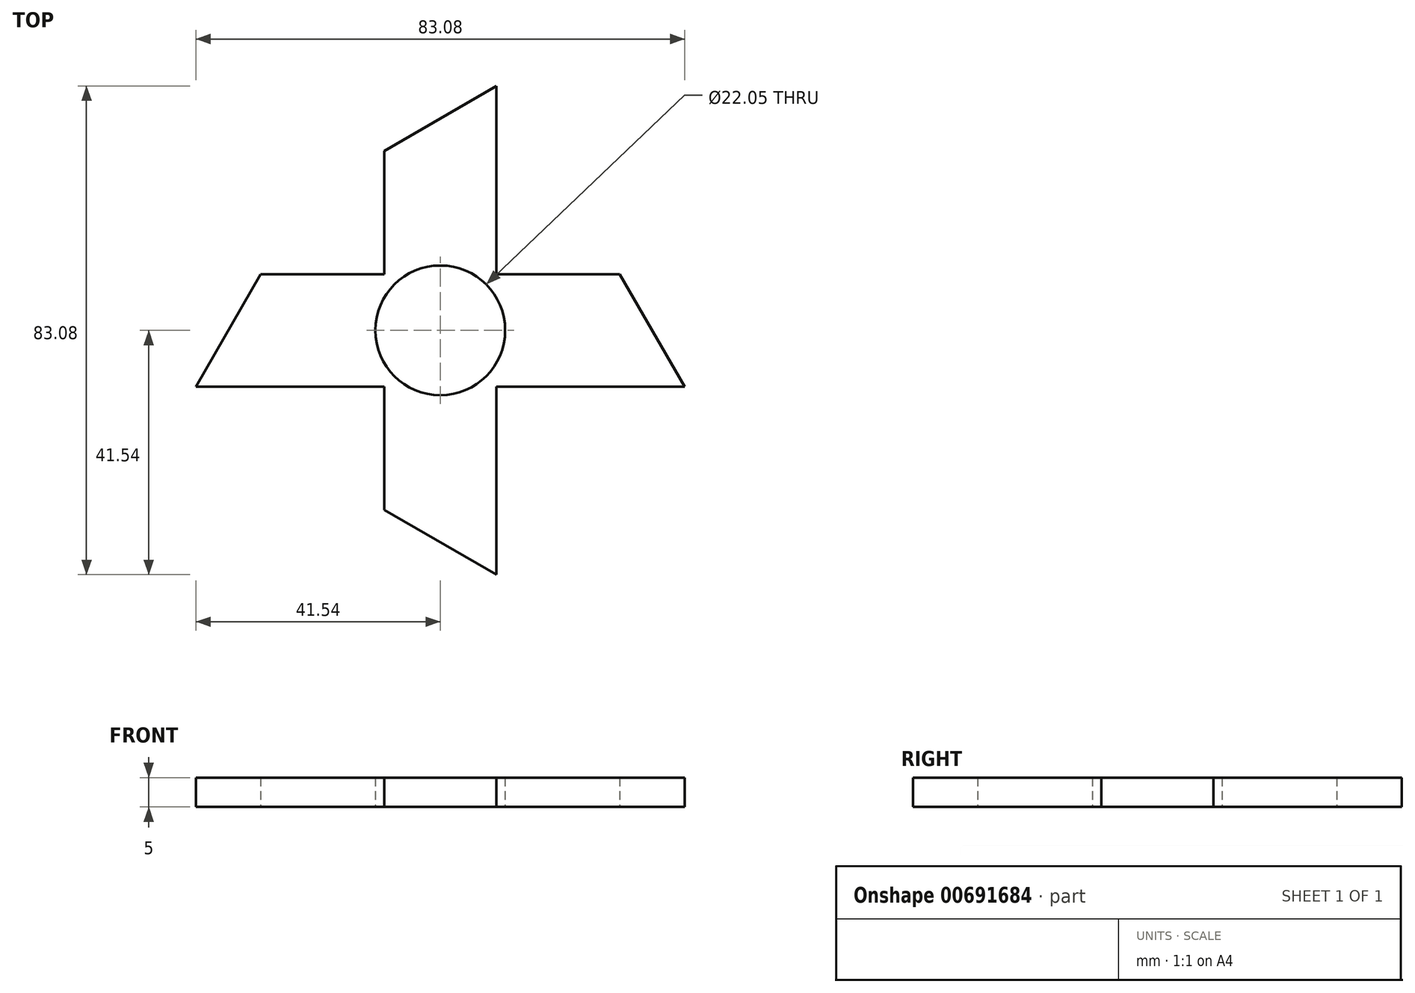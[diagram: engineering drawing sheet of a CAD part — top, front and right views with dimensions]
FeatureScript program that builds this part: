
annotation { "Feature Type Name" : "Feature", "Feature Type Description" : "" }
export const myFeature = defineFeature(function(context is Context, id is Id, definition is map)
    precondition{}
    {
        {
            var Q0;
            Q0=qCreatedBy(makeId("Top.planeOp"),FACE);
            var sketch = newSketch(context, id + "F0", { "sketchPlane" : qUnion([Q0])});
            skCircle(sketch, "E0", {"center": v(0, 0) * mm, "radius": 11.03 * mm});
            skLineSegment(sketch, "E1", {"start": v(0, 0) * mm, "end": v(0, 11.03) * mm});
            skLineSegment(sketch, "E2", {"start": v(-9.55, 5.51) * mm, "end": v(-9.55, 30.51) * mm});
            skPoint(sketch, "E2.startSnap0", {"position": v(0, 5.51) * mm});
            skLineSegment(sketch, "E3", {"start": v(9.55, 5.51) * mm, "end": v(9.55, 30.51) * mm});
            skLineSegment(sketch, "E4", {"start": v(-9.55, 30.51) * mm, "end": v(9.55, 30.51) * mm});
            skLineSegment(sketch, "E5.1.0", {"start": v(-5.51, 9.55) * mm, "end": v(-30.51, 9.55) * mm});
            skLineSegment(sketch, "E5.1.1", {"start": v(-30.51, -9.55) * mm, "end": v(-30.51, 9.55) * mm});
            skLineSegment(sketch, "E5.1.2", {"start": v(-5.51, -9.55) * mm, "end": v(-30.51, -9.55) * mm});
            skLineSegment(sketch, "E5.2.0", {"start": v(-9.55, -5.51) * mm, "end": v(-9.55, -30.51) * mm});
            skLineSegment(sketch, "E5.2.1", {"start": v(9.55, -30.51) * mm, "end": v(-9.55, -30.51) * mm});
            skLineSegment(sketch, "E5.2.2", {"start": v(9.55, -5.51) * mm, "end": v(9.55, -30.51) * mm});
            skLineSegment(sketch, "E5.3.0", {"start": v(5.51, -9.55) * mm, "end": v(30.51, -9.55) * mm});
            skLineSegment(sketch, "E5.3.1", {"start": v(30.51, 9.55) * mm, "end": v(30.51, -9.55) * mm});
            skLineSegment(sketch, "E5.3.2", {"start": v(5.51, 9.55) * mm, "end": v(30.51, 9.55) * mm});
            skLineSegment(sketch, "E6", {"start": v(-9.55, 30.51) * mm, "end": v(9.55, 41.54) * mm});
            skLineSegment(sketch, "E7", {"start": v(9.55, 41.54) * mm, "end": v(9.55, 30.51) * mm});
            skLineSegment(sketch, "E8", {"start": v(0, 36.02) * mm, "end": v(9.55, 41.54) * mm});
            skLineSegment(sketch, "E9", {"start": v(-30.51, -9.55) * mm, "end": v(-41.54, -9.55) * mm});
            skLineSegment(sketch, "E10", {"start": v(-41.54, -9.55) * mm, "end": v(-30.51, 9.55) * mm});
            skLineSegment(sketch, "E11", {"start": v(-36.03, 0) * mm, "end": v(-41.54, -9.55) * mm});
            skLineSegment(sketch, "E12.MirrorCS", {"start": v(41.54, -9.55) * mm, "end": v(30.51, 9.55) * mm});
            skLineSegment(sketch, "E13.MirrorCS", {"start": v(30.51, -9.55) * mm, "end": v(41.54, -9.55) * mm});
            skLineSegment(sketch, "E14", {"start": v(0, 0) * mm, "end": v(-3.92, 0) * mm});
            skLineSegment(sketch, "E15.MirrorCS", {"start": v(-9.55, -30.51) * mm, "end": v(9.55, -41.54) * mm});
            skLineSegment(sketch, "E16.MirrorCS", {"start": v(9.55, -41.54) * mm, "end": v(9.55, -30.51) * mm});
            skSolve(sketch);
        }
        {
            var Q0;
            {var subQ0=sQuery(id+"F0.wireOp",EDGE,"E4");Q0=makeQuery(id+"F0.imprint","IMPRINT",FACE,{"disambiguationData":[TD([[makeQuery(id+"F0.imprint","IMPRINT",EDGE,{"derivedFrom":subQ0}),-1.0]])]});}
            var Q1;
            Q1=makeQuery(id+"F0.imprint","IMPRINT",FACE,{"disambiguationData":[TD([[makeQuery(id+"F0.imprint","IMPRINT",EDGE,{"derivedFrom":sQuery(id+"F0.wireOp",EDGE,"E4")}),1.0]])]});
            var Q2;
            {var subQ0=sQuery(id+"F0.wireOp",EDGE,"E2");var subQ1=sQuery(id+"F0.wireOp",EDGE,"E0");var subQ2=makeQuery(id+"F0.imprint","INTERSECT",VERTEX,{"derivedFrom":[subQ1,subQ0]});Q2=makeQuery(id+"F0.imprint","IMPRINT",FACE,{"disambiguationData":[TD([[makeQuery(id+"F0.imprint","IMPRINT",EDGE,{"disambiguationData":[TD([[subQ2,1.0]])],"derivedFrom":subQ1}),-1.0]])]});}
            var Q3;
            {var subQ0=sQuery(id+"F0.wireOp",EDGE,"E5.1.1");Q3=makeQuery(id+"F0.imprint","IMPRINT",FACE,{"disambiguationData":[TD([[makeQuery(id+"F0.imprint","IMPRINT",EDGE,{"derivedFrom":subQ0}),-1.0]])]});}
            var Q4;
            Q4=makeQuery(id+"F0.imprint","IMPRINT",FACE,{"disambiguationData":[TD([[makeQuery(id+"F0.imprint","IMPRINT",EDGE,{"derivedFrom":sQuery(id+"F0.wireOp",EDGE,"E5.1.1")}),1.0]])]});
            var Q5;
            {var subQ0=sQuery(id+"F0.wireOp",EDGE,"E5.1.2");var subQ1=sQuery(id+"F0.wireOp",EDGE,"E0");var subQ2=makeQuery(id+"F0.imprint","INTERSECT",VERTEX,{"derivedFrom":[subQ1,subQ0]});Q5=makeQuery(id+"F0.imprint","IMPRINT",FACE,{"disambiguationData":[TD([[makeQuery(id+"F0.imprint","IMPRINT",EDGE,{"disambiguationData":[TD([[subQ2,1.0]])],"derivedFrom":subQ1}),-1.0]])]});}
            var Q6;
            {var subQ0=sQuery(id+"F0.wireOp",EDGE,"E5.2.1");Q6=makeQuery(id+"F0.imprint","IMPRINT",FACE,{"disambiguationData":[TD([[makeQuery(id+"F0.imprint","IMPRINT",EDGE,{"derivedFrom":subQ0}),-1.0]])]});}
            var Q7;
            Q7=makeQuery(id+"F0.imprint","IMPRINT",FACE,{"disambiguationData":[TD([[makeQuery(id+"F0.imprint","IMPRINT",EDGE,{"derivedFrom":sQuery(id+"F0.wireOp",EDGE,"E5.2.1")}),1.0]])]});
            var Q8;
            {var subQ0=sQuery(id+"F0.wireOp",EDGE,"E5.2.2");var subQ1=sQuery(id+"F0.wireOp",EDGE,"E0");var subQ2=makeQuery(id+"F0.imprint","INTERSECT",VERTEX,{"derivedFrom":[subQ1,subQ0]});Q8=makeQuery(id+"F0.imprint","IMPRINT",FACE,{"disambiguationData":[TD([[makeQuery(id+"F0.imprint","IMPRINT",EDGE,{"disambiguationData":[TD([[subQ2,1.0]])],"derivedFrom":subQ1}),-1.0]])]});}
            var Q9;
            {var subQ0=sQuery(id+"F0.wireOp",EDGE,"E3");var subQ1=sQuery(id+"F0.wireOp",EDGE,"E0");var subQ2=makeQuery(id+"F0.imprint","INTERSECT",VERTEX,{"derivedFrom":[subQ1,subQ0]});Q9=makeQuery(id+"F0.imprint","IMPRINT",FACE,{"disambiguationData":[TD([[makeQuery(id+"F0.imprint","IMPRINT",EDGE,{"disambiguationData":[TD([[subQ2,-1.0]])],"derivedFrom":subQ1}),-1.0]])]});}
            var Q10;
            {var subQ0=sQuery(id+"F0.wireOp",EDGE,"E5.3.1");Q10=makeQuery(id+"F0.imprint","IMPRINT",FACE,{"disambiguationData":[TD([[makeQuery(id+"F0.imprint","IMPRINT",EDGE,{"derivedFrom":subQ0}),-1.0]])]});}
            var Q11;
            Q11=makeQuery(id+"F0.imprint","IMPRINT",FACE,{"disambiguationData":[TD([[makeQuery(id+"F0.imprint","IMPRINT",EDGE,{"derivedFrom":sQuery(id+"F0.wireOp",EDGE,"E5.3.1")}),1.0]])]});
            extrude(context, id + "F1", {"entities" : qUnion([Q0, Q1, Q2, Q3, Q4, Q5, Q6, Q7, Q8, Q9, Q10, Q11]), "depth" : 5 * mm, "offsetDistance" : 25 * mm});
        }
    });
